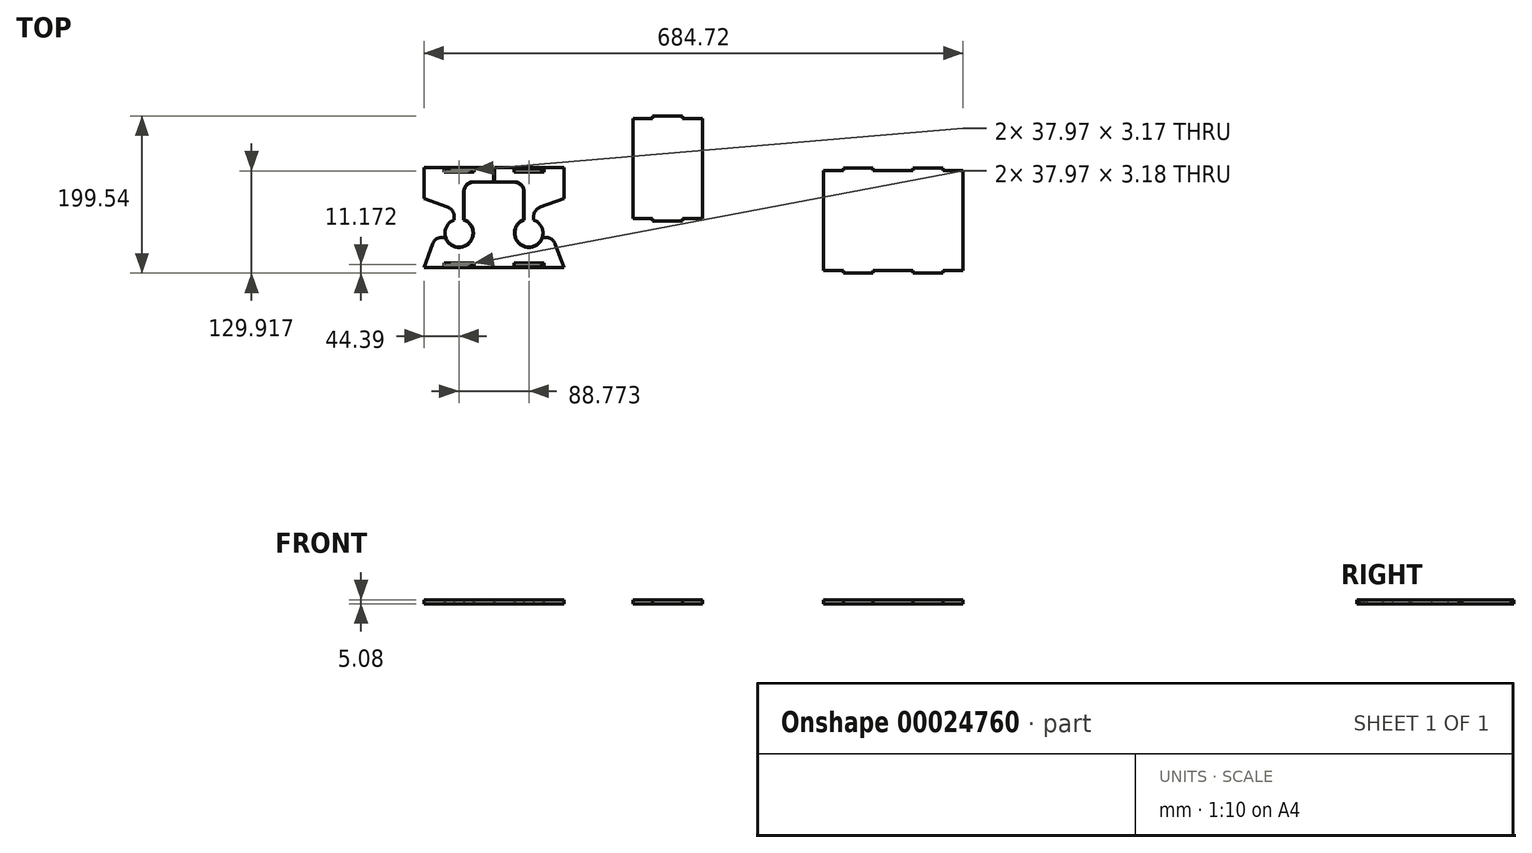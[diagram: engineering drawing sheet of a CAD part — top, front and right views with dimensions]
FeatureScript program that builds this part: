
annotation { "Feature Type Name" : "Feature", "Feature Type Description" : "" }
export const myFeature = defineFeature(function(context is Context, id is Id, definition is map)
    precondition{}
    {
        {
            var Q0;
            Q0=qCreatedBy(makeId("Top.planeOp"),FACE);
            var sketch = newSketch(context, id + "F0", { "sketchPlane" : qUnion([Q0])});
            skLineSegment(sketch, "E0.bottom", {"start": v(44.39, -63.94) * mm, "end": v(-44.39, -63.94) * mm});
            skLineSegment(sketch, "E0.top", {"start": v(43.88, 63.06) * mm, "end": v(-44.39, 63.06) * mm});
            skLineSegment(sketch, "E0.left", {"start": v(44.39, -63.94) * mm, "end": v(44.39, 44.53) * mm, "construction": true});
            skLineSegment(sketch, "E0.right", {"start": v(-44.39, 23.67) * mm, "end": v(-44.39, 63.06) * mm});
            skArc(sketch, "E1", {"start": v(-5.94, -3.24) * mm, "mid": v(0, -37.83) * mm, "end": v(5.94, -3.24) * mm});
            skLineSegment(sketch, "E2", {"start": v(5.94, -3.24) * mm, "end": v(5.94, 32.34) * mm});
            skLineSegment(sketch, "E3", {"start": v(18.64, 45.04) * mm, "end": v(43.88, 45.04) * mm});
            skLineSegment(sketch, "E4", {"start": v(-5.94, -3.24) * mm, "end": v(-5.94, 0.78) * mm});
            skLineSegment(sketch, "E5", {"start": v(-14.3, 12.72) * mm, "end": v(-44.39, 23.67) * mm});
            skLineSegment(sketch, "E6", {"start": v(-44.39, -63.94) * mm, "end": v(-33.44, -33.85) * mm});
            skLineSegment(sketch, "E7", {"start": v(-21.5, -25.5) * mm, "end": v(-17.48, -25.5) * mm});
            skPoint(sketch, "E8.visualSharp", {"position": v(-5.94, 9.68) * mm});
            skArc(sketch, "E8.filletArc", {"start": v(-5.94, 0.78) * mm, "mid": v(-8.24, 8.07) * mm, "end": v(-14.3, 12.72) * mm});
            skPoint(sketch, "E9.visualSharp", {"position": v(-30.4, -25.5) * mm});
            skArc(sketch, "E9.filletArc", {"start": v(-21.5, -25.5) * mm, "mid": v(-28.79, -27.79) * mm, "end": v(-33.44, -33.85) * mm});
            skPoint(sketch, "E10.visualSharp", {"position": v(5.94, 45.04) * mm});
            skArc(sketch, "E10.filletArc", {"start": v(18.64, 45.04) * mm, "mid": v(9.66, 41.32) * mm, "end": v(5.94, 32.34) * mm});
            skArc(sketch, "E11", {"start": v(-16.94, -25.5) * mm, "mid": v(12.41, -32.79) * mm, "end": v(5.94, -3.24) * mm});
            skLineSegment(sketch, "E12.0", {"start": v(18.64, 44.53) * mm, "end": v(44.39, 44.53) * mm});
            skArc(sketch, "E12.1", {"start": v(18.64, 44.53) * mm, "mid": v(10.02, 40.96) * mm, "end": v(6.45, 32.34) * mm});
            skLineSegment(sketch, "E12.2", {"start": v(6.45, -2.89) * mm, "end": v(6.45, 32.34) * mm});
            skArc(sketch, "E12.3", {"start": v(-17.48, -25.5) * mm, "mid": v(12.58, -33.33) * mm, "end": v(6.45, -2.89) * mm});
            skLineSegment(sketch, "E13.bottom", {"start": v(-18.99, -61.4) * mm, "end": v(18.99, -61.4) * mm});
            skLineSegment(sketch, "E13.top", {"start": v(-18.99, -58.22) * mm, "end": v(18.99, -58.22) * mm});
            skLineSegment(sketch, "E13.left", {"start": v(-18.99, -61.4) * mm, "end": v(-18.99, -58.22) * mm});
            skLineSegment(sketch, "E13.right", {"start": v(18.99, -61.4) * mm, "end": v(18.99, -58.22) * mm});
            skLineSegment(sketch, "E14.bottom", {"start": v(-18.99, 60.52) * mm, "end": v(18.99, 60.52) * mm});
            skLineSegment(sketch, "E14.top", {"start": v(-18.99, 57.35) * mm, "end": v(18.99, 57.35) * mm});
            skLineSegment(sketch, "E14.left", {"start": v(-18.99, 60.52) * mm, "end": v(-18.99, 57.35) * mm});
            skLineSegment(sketch, "E14.right", {"start": v(18.99, 60.52) * mm, "end": v(18.99, 57.35) * mm});
            skLineSegment(sketch, "E15", {"start": v(0, 57.35) * mm, "end": v(0, -61.4) * mm, "construction": true});
            skLineSegment(sketch, "E16", {"start": v(43.88, 45.04) * mm, "end": v(43.88, 63.06) * mm});
            skLineSegment(sketch, "E17.MirrorCS", {"start": v(107.76, 57.35) * mm, "end": v(69.79, 57.35) * mm});
            skLineSegment(sketch, "E18.MirrorCS", {"start": v(107.76, -61.4) * mm, "end": v(107.76, -58.22) * mm});
            skLineSegment(sketch, "E19.MirrorCS", {"start": v(107.76, 60.52) * mm, "end": v(107.76, 57.35) * mm});
            skArc(sketch, "E20.MirrorCS", {"start": v(106.25, -25.5) * mm, "mid": v(76.2, -33.33) * mm, "end": v(82.32, -2.89) * mm});
            skLineSegment(sketch, "E21.MirrorCS", {"start": v(133.16, 23.67) * mm, "end": v(133.16, 63.06) * mm});
            skLineSegment(sketch, "E22.MirrorCS", {"start": v(69.79, -61.4) * mm, "end": v(69.79, -58.22) * mm});
            skLineSegment(sketch, "E23.MirrorCS", {"start": v(107.76, -61.4) * mm, "end": v(69.79, -61.4) * mm});
            skLineSegment(sketch, "E24.MirrorCS", {"start": v(82.32, -2.89) * mm, "end": v(82.32, 32.34) * mm});
            skLineSegment(sketch, "E25.MirrorCS", {"start": v(44.9, 45.04) * mm, "end": v(44.9, 63.06) * mm});
            skLineSegment(sketch, "E26.MirrorCS", {"start": v(88.77, 57.35) * mm, "end": v(88.77, -61.4) * mm, "construction": true});
            skLineSegment(sketch, "E27.MirrorCS", {"start": v(107.76, -58.22) * mm, "end": v(69.79, -58.22) * mm});
            skPoint(sketch, "E28.MirrorP", {"position": v(119.17, -25.5) * mm});
            skArc(sketch, "E29.MirrorCS", {"start": v(70.13, 45.04) * mm, "mid": v(79.1, 41.32) * mm, "end": v(82.83, 32.34) * mm});
            skArc(sketch, "E30.MirrorCS", {"start": v(105.5, -13.91) * mm, "mid": v(81.19, -36.13) * mm, "end": v(82.83, -3.24) * mm});
            skLineSegment(sketch, "E31.MirrorCS", {"start": v(70.13, 45.04) * mm, "end": v(44.9, 45.04) * mm});
            skLineSegment(sketch, "E32.MirrorCS", {"start": v(110.27, -25.5) * mm, "end": v(106.25, -25.5) * mm});
            skLineSegment(sketch, "E33.MirrorCS", {"start": v(44.39, -63.94) * mm, "end": v(133.16, -63.94) * mm});
            skPoint(sketch, "E34.MirrorP", {"position": v(94.72, 9.68) * mm});
            skArc(sketch, "E35.MirrorCS", {"start": v(94.72, -3.24) * mm, "mid": v(88.77, -37.83) * mm, "end": v(82.83, -3.24) * mm});
            skLineSegment(sketch, "E36.MirrorCS", {"start": v(107.76, 60.52) * mm, "end": v(69.79, 60.52) * mm});
            skLineSegment(sketch, "E37.MirrorCS", {"start": v(133.16, -63.94) * mm, "end": v(122.2, -33.85) * mm});
            skArc(sketch, "E38.MirrorCS", {"start": v(94.72, 0.78) * mm, "mid": v(97.01, 8.07) * mm, "end": v(103.07, 12.72) * mm});
            skPoint(sketch, "E39.MirrorP", {"position": v(82.83, 45.04) * mm});
            skArc(sketch, "E40.MirrorCS", {"start": v(110.27, -25.5) * mm, "mid": v(117.56, -27.79) * mm, "end": v(122.2, -33.85) * mm});
            skLineSegment(sketch, "E41.MirrorCS", {"start": v(69.79, 60.52) * mm, "end": v(69.79, 57.35) * mm});
            skLineSegment(sketch, "E42.MirrorCS", {"start": v(94.72, -3.24) * mm, "end": v(94.72, 0.78) * mm});
            skLineSegment(sketch, "E43.MirrorCS", {"start": v(70.13, 44.53) * mm, "end": v(44.39, 44.53) * mm});
            skLineSegment(sketch, "E44.MirrorCS", {"start": v(82.83, -3.24) * mm, "end": v(82.83, 32.34) * mm});
            skLineSegment(sketch, "E45.MirrorCS", {"start": v(44.9, 63.06) * mm, "end": v(133.16, 63.06) * mm});
            skLineSegment(sketch, "E46.MirrorCS", {"start": v(103.07, 12.72) * mm, "end": v(133.16, 23.67) * mm});
            skArc(sketch, "E47.MirrorCS", {"start": v(70.13, 44.53) * mm, "mid": v(78.75, 40.96) * mm, "end": v(82.32, 32.34) * mm});
            skLineSegment(sketch, "E48.bottom", {"start": v(246.01, 128.56) * mm, "end": v(284.24, 128.56) * mm});
            skLineSegment(sketch, "E48.top", {"start": v(246.01, -4.79) * mm, "end": v(284.24, -4.79) * mm});
            skLineSegment(sketch, "E48.left", {"start": v(220.93, 125.39) * mm, "end": v(220.93, -1.61) * mm});
            skLineSegment(sketch, "E48.right", {"start": v(309.32, 125.39) * mm, "end": v(309.32, -1.61) * mm});
            skLineSegment(sketch, "E49.left", {"start": v(246.01, 128.56) * mm, "end": v(246.01, 125.39) * mm});
            skLineSegment(sketch, "E49.right", {"start": v(284.24, 128.56) * mm, "end": v(284.24, 125.39) * mm});
            skPoint(sketch, "E50", {"position": v(265.13, 128.56) * mm});
            skLineSegment(sketch, "E51", {"start": v(246.01, 125.39) * mm, "end": v(220.93, 125.39) * mm});
            skLineSegment(sketch, "E52", {"start": v(220.93, 125.39) * mm, "end": v(246.01, 125.39) * mm});
            skLineSegment(sketch, "E53", {"start": v(220.93, 61.89) * mm, "end": v(309.32, 61.89) * mm, "construction": true});
            skPoint(sketch, "E54.orphan", {"position": v(220.93, 128.56) * mm});
            skLineSegment(sketch, "E55.trimOffspring", {"start": v(284.24, 125.39) * mm, "end": v(309.32, 125.39) * mm});
            skPoint(sketch, "E56.orphan", {"position": v(309.32, 128.56) * mm});
            skLineSegment(sketch, "E57.MirrorCS", {"start": v(284.24, -4.79) * mm, "end": v(284.24, -1.61) * mm});
            skLineSegment(sketch, "E58.MirrorCS", {"start": v(246.01, -4.79) * mm, "end": v(246.01, -1.61) * mm});
            skPoint(sketch, "E59.MirrorP", {"position": v(265.13, -4.79) * mm});
            skLineSegment(sketch, "E60.MirrorCS", {"start": v(220.93, -1.61) * mm, "end": v(246.01, -1.61) * mm});
            skLineSegment(sketch, "E61.MirrorCS", {"start": v(246.01, -1.61) * mm, "end": v(220.93, -1.61) * mm});
            skPoint(sketch, "E62.MirrorP", {"position": v(220.93, -4.79) * mm});
            skLineSegment(sketch, "E63.MirrorCS", {"start": v(309.32, -1.61) * mm, "end": v(309.32, 125.39) * mm});
            skLineSegment(sketch, "E64.MirrorCS", {"start": v(284.24, -1.61) * mm, "end": v(309.32, -1.61) * mm});
            skLineSegment(sketch, "E65.MirrorCS", {"start": v(220.93, -1.61) * mm, "end": v(220.93, 125.39) * mm});
            skPoint(sketch, "E66.MirrorP", {"position": v(309.32, -4.79) * mm});
            skPoint(sketch, "E67.MirrorP", {"position": v(462.78, -70.98) * mm});
            skPoint(sketch, "E68.MirrorP", {"position": v(507.17, -70.98) * mm});
            skLineSegment(sketch, "E69", {"start": v(462.78, -4.3) * mm, "end": v(551.56, -4.3) * mm, "construction": true});
            skLineSegment(sketch, "E70.MirrorCS", {"start": v(488.18, -70.98) * mm, "end": v(526.16, -70.98) * mm});
            skPoint(sketch, "E71.MirrorP", {"position": v(551.56, -70.98) * mm});
            skLineSegment(sketch, "E72.MirrorCS", {"start": v(526.16, -67.8) * mm, "end": v(551.56, -67.8) * mm});
            skLineSegment(sketch, "E73.right", {"start": v(551.56, 59.2) * mm, "end": v(551.56, -67.8) * mm, "construction": true});
            skLineSegment(sketch, "E74.MirrorCS", {"start": v(462.78, -67.8) * mm, "end": v(462.78, 59.2) * mm});
            skLineSegment(sketch, "E75.trimOffspring", {"start": v(526.16, 59.2) * mm, "end": v(551.56, 59.2) * mm});
            skPoint(sketch, "E76.orphan", {"position": v(551.56, 62.37) * mm});
            skPoint(sketch, "E77.orphan", {"position": v(462.78, 62.37) * mm});
            skPoint(sketch, "E78", {"position": v(507.17, 62.37) * mm});
            skLineSegment(sketch, "E79.MirrorCS", {"start": v(462.78, -67.8) * mm, "end": v(488.18, -67.8) * mm});
            skLineSegment(sketch, "E80", {"start": v(488.18, 59.2) * mm, "end": v(462.78, 59.2) * mm});
            skLineSegment(sketch, "E73.bottom", {"start": v(488.18, 62.37) * mm, "end": v(526.16, 62.37) * mm});
            skLineSegment(sketch, "E73.left", {"start": v(462.78, 59.2) * mm, "end": v(462.78, -67.8) * mm});
            skLineSegment(sketch, "E81.MirrorCS", {"start": v(551.56, -67.8) * mm, "end": v(551.56, 59.2) * mm, "construction": true});
            skLineSegment(sketch, "E82", {"start": v(462.78, 59.2) * mm, "end": v(488.18, 59.2) * mm});
            skLineSegment(sketch, "E83.MirrorCS", {"start": v(488.18, -67.8) * mm, "end": v(462.78, -67.8) * mm});
            skLineSegment(sketch, "E84.left", {"start": v(488.18, 62.37) * mm, "end": v(488.18, 59.2) * mm});
            skLineSegment(sketch, "E84.right", {"start": v(526.16, 62.37) * mm, "end": v(526.16, 59.2) * mm});
            skLineSegment(sketch, "E85.MirrorCS", {"start": v(488.18, -67.8) * mm, "end": v(488.18, -70.98) * mm});
            skLineSegment(sketch, "E86.MirrorCS", {"start": v(526.16, -67.8) * mm, "end": v(526.16, -70.98) * mm});
            skLineSegment(sketch, "E87.MirrorCS", {"start": v(576.96, -70.98) * mm, "end": v(576.96, -67.8) * mm});
            skLineSegment(sketch, "E88.MirrorCS", {"start": v(614.93, -70.98) * mm, "end": v(614.93, -67.8) * mm});
            skLineSegment(sketch, "E89.MirrorCS", {"start": v(576.96, 62.37) * mm, "end": v(576.96, 59.2) * mm});
            skLineSegment(sketch, "E90.MirrorCS", {"start": v(614.93, 62.37) * mm, "end": v(614.93, 59.2) * mm});
            skLineSegment(sketch, "E91.MirrorCS", {"start": v(614.93, -70.98) * mm, "end": v(576.96, -70.98) * mm});
            skLineSegment(sketch, "E92.MirrorCS", {"start": v(640.33, 59.2) * mm, "end": v(640.33, -67.8) * mm});
            skPoint(sketch, "E93.MirrorP", {"position": v(640.33, -70.98) * mm});
            skLineSegment(sketch, "E94.MirrorCS", {"start": v(614.93, 62.37) * mm, "end": v(576.96, 62.37) * mm});
            skLineSegment(sketch, "E95.MirrorCS", {"start": v(640.33, 59.2) * mm, "end": v(614.93, 59.2) * mm});
            skPoint(sketch, "E96.MirrorP", {"position": v(595.94, 62.37) * mm});
            skLineSegment(sketch, "E97.MirrorCS", {"start": v(614.93, -67.8) * mm, "end": v(640.33, -67.8) * mm});
            skPoint(sketch, "E98.MirrorP", {"position": v(595.94, -70.98) * mm});
            skLineSegment(sketch, "E99.MirrorCS", {"start": v(576.96, -67.8) * mm, "end": v(551.56, -67.8) * mm});
            skPoint(sketch, "E100.MirrorP", {"position": v(640.33, 62.37) * mm});
            skLineSegment(sketch, "E101.MirrorCS", {"start": v(640.33, -67.8) * mm, "end": v(640.33, 59.2) * mm});
            skLineSegment(sketch, "E102.MirrorCS", {"start": v(614.93, 59.2) * mm, "end": v(640.33, 59.2) * mm});
            skLineSegment(sketch, "E103.MirrorCS", {"start": v(640.33, -67.8) * mm, "end": v(614.93, -67.8) * mm});
            skLineSegment(sketch, "E104.MirrorCS", {"start": v(640.33, -4.3) * mm, "end": v(551.56, -4.3) * mm, "construction": true});
            skLineSegment(sketch, "E105.MirrorCS", {"start": v(576.96, 59.2) * mm, "end": v(551.56, 59.2) * mm});
            skPoint(sketch, "E106", {"position": v(104.67, -28.03) * mm});
            skLineSegment(sketch, "E107.trimOffspring", {"start": v(322.72, -47.2) * mm, "end": v(347.8, -47.2) * mm});
            skPoint(sketch, "E108.orphan", {"position": v(347.8, -177.38) * mm});
            skLineSegment(sketch, "E109.MirrorCS", {"start": v(322.72, -174.2) * mm, "end": v(347.8, -174.2) * mm});
            skPoint(sketch, "E110.orphan", {"position": v(259.4, -44.03) * mm});
            skLineSegment(sketch, "E111.MirrorCS", {"start": v(259.4, -174.2) * mm, "end": v(259.4, -47.2) * mm});
            skPoint(sketch, "E112", {"position": v(303.6, -44.03) * mm});
            skPoint(sketch, "E113.orphan", {"position": v(347.8, -44.03) * mm});
            skLineSegment(sketch, "E114.MirrorCS", {"start": v(284.49, -177.38) * mm, "end": v(322.72, -177.38) * mm});
            skLineSegment(sketch, "E115.MirrorCS", {"start": v(284.49, -174.2) * mm, "end": v(259.4, -174.2) * mm});
            skPoint(sketch, "E116.MirrorP", {"position": v(259.4, -177.38) * mm});
            skLineSegment(sketch, "E117", {"start": v(259.4, -47.2) * mm, "end": v(284.49, -47.2) * mm});
            skLineSegment(sketch, "E118.bottom", {"start": v(284.49, -44.03) * mm, "end": v(322.72, -44.03) * mm});
            skLineSegment(sketch, "E119.MirrorCS", {"start": v(347.8, -174.2) * mm, "end": v(347.8, -47.2) * mm});
            skPoint(sketch, "E120.MirrorP", {"position": v(303.6, -177.38) * mm});
            skLineSegment(sketch, "E121", {"start": v(259.4, -110.7) * mm, "end": v(347.8, -110.7) * mm, "construction": true});
            skLineSegment(sketch, "E118.left", {"start": v(259.4, -47.2) * mm, "end": v(259.4, -174.2) * mm});
            skLineSegment(sketch, "E118.right", {"start": v(347.8, -47.2) * mm, "end": v(347.8, -174.2) * mm});
            skLineSegment(sketch, "E122.MirrorCS", {"start": v(259.4, -174.2) * mm, "end": v(284.49, -174.2) * mm});
            skLineSegment(sketch, "E123", {"start": v(284.49, -47.2) * mm, "end": v(259.4, -47.2) * mm});
            skLineSegment(sketch, "E124.MirrorCS", {"start": v(322.72, -177.38) * mm, "end": v(322.72, -174.2) * mm});
            skLineSegment(sketch, "E125.left", {"start": v(284.49, -44.03) * mm, "end": v(284.49, -47.2) * mm});
            skLineSegment(sketch, "E126.MirrorCS", {"start": v(284.49, -177.38) * mm, "end": v(284.49, -174.2) * mm});
            skLineSegment(sketch, "E125.right", {"start": v(322.72, -44.03) * mm, "end": v(322.72, -47.2) * mm});
            skLineSegment(sketch, "E127.MirrorCS", {"start": v(-22.32, -274.1) * mm, "end": v(-60.3, -274.1) * mm});
            skLineSegment(sketch, "E128.MirrorCS", {"start": v(-27, -203.24) * mm, "end": v(3.22, -192.24) * mm});
            skArc(sketch, "E129.MirrorCS", {"start": v(-23.78, -241.23) * mm, "mid": v(-53.77, -249.37) * mm, "end": v(-47.76, -218.88) * mm});
            skPoint(sketch, "E130.MirrorP", {"position": v(-10.83, -241.23) * mm});
            skLineSegment(sketch, "E131.MirrorCS", {"start": v(-22.32, -158.52) * mm, "end": v(-60.3, -158.52) * mm});
            skArc(sketch, "E132.MirrorCS", {"start": v(-35.36, -219.24) * mm, "mid": v(-41.3, -253.78) * mm, "end": v(-47.25, -219.24) * mm});
            skArc(sketch, "E133.3", {"start": v(-147.6, -241.23) * mm, "mid": v(-117.6, -249.37) * mm, "end": v(-123.63, -218.88) * mm});
            skLineSegment(sketch, "E134.MirrorCS", {"start": v(-22.32, -155.35) * mm, "end": v(-60.3, -155.35) * mm});
            skLineSegment(sketch, "E135.MirrorCS", {"start": v(-59.95, -170.95) * mm, "end": v(-85.18, -170.95) * mm});
            skLineSegment(sketch, "E136.MirrorCS", {"start": v(-85.7, -279.8) * mm, "end": v(3.22, -279.8) * mm});
            skLineSegment(sketch, "E137", {"start": v(-86.2, -170.95) * mm, "end": v(-86.2, -152.8) * mm});
            skPoint(sketch, "E138.MirrorP", {"position": v(-35.36, -206.28) * mm});
            skLineSegment(sketch, "E139.MirrorCS", {"start": v(-41.3, -158.52) * mm, "end": v(-41.3, -277.27) * mm, "construction": true});
            skLineSegment(sketch, "E140.MirrorCS", {"start": v(-85.18, -152.8) * mm, "end": v(3.22, -152.8) * mm});
            skLineSegment(sketch, "E133.2", {"start": v(-123.63, -218.88) * mm, "end": v(-123.63, -183.65) * mm});
            skPoint(sketch, "E141.visualSharp", {"position": v(-136.02, -206.28) * mm});
            skLineSegment(sketch, "E142", {"start": v(-130.08, -158.52) * mm, "end": v(-130.08, -277.27) * mm, "construction": true});
            skLineSegment(sketch, "E143.bottom", {"start": v(-149.06, -155.35) * mm, "end": v(-111.1, -155.35) * mm});
            skPoint(sketch, "E144", {"position": v(-25.43, -244) * mm});
            skLineSegment(sketch, "E143.top", {"start": v(-149.06, -158.52) * mm, "end": v(-111.1, -158.52) * mm});
            skLineSegment(sketch, "E145.MirrorCS", {"start": v(-85.18, -170.95) * mm, "end": v(-85.18, -152.8) * mm});
            skLineSegment(sketch, "E146.MirrorCS", {"start": v(-47.25, -219.24) * mm, "end": v(-47.25, -183.65) * mm});
            skPoint(sketch, "E147.visualSharp", {"position": v(-124.13, -170.95) * mm});
            skLineSegment(sketch, "E148.top", {"start": v(-149.06, -274.1) * mm, "end": v(-111.1, -274.1) * mm});
            skLineSegment(sketch, "E149.MirrorCS", {"start": v(-22.32, -277.27) * mm, "end": v(-60.3, -277.27) * mm});
            skLineSegment(sketch, "E148.bottom", {"start": v(-149.06, -277.27) * mm, "end": v(-111.1, -277.27) * mm});
            skPoint(sketch, "E150.visualSharp", {"position": v(-160.56, -241.23) * mm});
            skLineSegment(sketch, "E151.MirrorCS", {"start": v(3.22, -192.24) * mm, "end": v(3.22, -152.8) * mm});
            skPoint(sketch, "E152.MirrorP", {"position": v(-47.25, -170.95) * mm});
            skLineSegment(sketch, "E153", {"start": v(-174.6, -279.8) * mm, "end": v(-163.6, -249.59) * mm});
            skLineSegment(sketch, "E154", {"start": v(-144.38, -203.24) * mm, "end": v(-174.6, -192.24) * mm});
            skArc(sketch, "E155", {"start": v(-136.02, -219.24) * mm, "mid": v(-130.08, -253.78) * mm, "end": v(-124.13, -219.24) * mm});
            skLineSegment(sketch, "E156.right", {"start": v(-174.6, -192.24) * mm, "end": v(-174.6, -152.8) * mm});
            skLineSegment(sketch, "E156.left", {"start": v(-85.7, -279.8) * mm, "end": v(-85.7, -171.46) * mm, "construction": true});
            skLineSegment(sketch, "E156.top", {"start": v(-86.2, -152.8) * mm, "end": v(-174.6, -152.8) * mm});
            skLineSegment(sketch, "E156.bottom", {"start": v(-85.7, -279.8) * mm, "end": v(-174.6, -279.8) * mm});
            skLineSegment(sketch, "E157.MirrorCS", {"start": v(3.22, -279.8) * mm, "end": v(-7.78, -249.59) * mm});
            skArc(sketch, "E158.MirrorCS", {"start": v(-35.36, -215.18) * mm, "mid": v(-33.06, -207.9) * mm, "end": v(-27, -203.24) * mm});
            skArc(sketch, "E133.1", {"start": v(-111.43, -171.46) * mm, "mid": v(-120.05, -175.03) * mm, "end": v(-123.63, -183.65) * mm});
            skLineSegment(sketch, "E159", {"start": v(-111.43, -170.95) * mm, "end": v(-86.2, -170.95) * mm});
            skArc(sketch, "E160.MirrorCS", {"start": v(-24.6, -229.9) * mm, "mid": v(-48.87, -252.08) * mm, "end": v(-47.25, -219.24) * mm});
            skArc(sketch, "E161.MirrorCS", {"start": v(-59.95, -170.95) * mm, "mid": v(-50.97, -174.67) * mm, "end": v(-47.25, -183.65) * mm});
            skLineSegment(sketch, "E162.MirrorCS", {"start": v(-47.76, -218.88) * mm, "end": v(-47.76, -183.65) * mm});
            skLineSegment(sketch, "E163.MirrorCS", {"start": v(-59.95, -171.46) * mm, "end": v(-85.7, -171.46) * mm});
            skArc(sketch, "E164.MirrorCS", {"start": v(-19.72, -241.23) * mm, "mid": v(-12.43, -243.53) * mm, "end": v(-7.78, -249.59) * mm});
            skLineSegment(sketch, "E165", {"start": v(-124.13, -219.24) * mm, "end": v(-124.13, -183.65) * mm});
            skArc(sketch, "E166", {"start": v(-147.07, -241.23) * mm, "mid": v(-117.77, -248.83) * mm, "end": v(-124.13, -219.24) * mm});
            skArc(sketch, "E147.filletArc", {"start": v(-111.43, -170.95) * mm, "mid": v(-120.41, -174.67) * mm, "end": v(-124.13, -183.65) * mm});
            skLineSegment(sketch, "E167.MirrorCS", {"start": v(-60.3, -155.35) * mm, "end": v(-60.3, -158.52) * mm});
            skLineSegment(sketch, "E168.MirrorCS", {"start": v(-22.32, -277.27) * mm, "end": v(-22.32, -274.1) * mm});
            skLineSegment(sketch, "E143.right", {"start": v(-111.1, -155.35) * mm, "end": v(-111.1, -158.52) * mm});
            skLineSegment(sketch, "E143.left", {"start": v(-149.06, -155.35) * mm, "end": v(-149.06, -158.52) * mm});
            skArc(sketch, "E169.MirrorCS", {"start": v(-59.95, -171.46) * mm, "mid": v(-51.33, -175.03) * mm, "end": v(-47.76, -183.65) * mm});
            skLineSegment(sketch, "E148.left", {"start": v(-149.06, -277.27) * mm, "end": v(-149.06, -274.1) * mm});
            skLineSegment(sketch, "E170.MirrorCS", {"start": v(-35.36, -219.24) * mm, "end": v(-35.36, -215.18) * mm});
            skLineSegment(sketch, "E171.MirrorCS", {"start": v(-60.3, -277.27) * mm, "end": v(-60.3, -274.1) * mm});
            skArc(sketch, "E150.filletArc", {"start": v(-151.66, -241.23) * mm, "mid": v(-158.95, -243.53) * mm, "end": v(-163.6, -249.59) * mm});
            skArc(sketch, "E141.filletArc", {"start": v(-136.02, -215.18) * mm, "mid": v(-138.32, -207.9) * mm, "end": v(-144.38, -203.24) * mm});
            skLineSegment(sketch, "E133.0", {"start": v(-111.43, -171.46) * mm, "end": v(-85.7, -171.46) * mm});
            skLineSegment(sketch, "E172.MirrorCS", {"start": v(-22.32, -155.35) * mm, "end": v(-22.32, -158.52) * mm});
            skLineSegment(sketch, "E173.MirrorCS", {"start": v(-19.72, -241.23) * mm, "end": v(-23.78, -241.23) * mm});
            skLineSegment(sketch, "E148.right", {"start": v(-111.1, -277.27) * mm, "end": v(-111.1, -274.1) * mm});
            skLineSegment(sketch, "E174", {"start": v(-151.66, -241.23) * mm, "end": v(-147.6, -241.23) * mm});
            skLineSegment(sketch, "E175", {"start": v(-136.02, -219.24) * mm, "end": v(-136.02, -215.18) * mm});
            skSolve(sketch);
        }
        {
            var Q0;
            Q0=makeQuery(id+"F0.imprint","IMPRINT",FACE,{"disambiguationData":[TD([[makeQuery(id+"F0.imprint","IMPRINT",EDGE,{"derivedFrom":sQuery(id+"F0.wireOp",EDGE,"E0.bottom")}),-1.0]])]});
            var Q1;
            Q1=makeQuery(id+"F0.imprint","IMPRINT",FACE,{"disambiguationData":[TD([[makeQuery(id+"F0.imprint","IMPRINT",EDGE,{"derivedFrom":sQuery(id+"F0.wireOp",EDGE,"E17.MirrorCS")}),1.0]])]});
            var Q2;
            Q2=makeQuery(id+"F0.imprint","IMPRINT",FACE,{"disambiguationData":[TD([[makeQuery(id+"F0.imprint","IMPRINT",EDGE,{"derivedFrom":sQuery(id+"F0.wireOp",EDGE,"E0.top")}),1.0]])]});
            var Q3;
            Q3=makeQuery(id+"F0.imprint","IMPRINT",FACE,{"disambiguationData":[TD([[makeQuery(id+"F0.imprint","IMPRINT",EDGE,{"derivedFrom":sQuery(id+"F0.wireOp",EDGE,"E48.bottom")}),-1.0]])]});
            var Q4;
            Q4=makeQuery(id+"F0.imprint","IMPRINT",FACE,{"disambiguationData":[TD([[makeQuery(id+"F0.imprint","IMPRINT",EDGE,{"derivedFrom":sQuery(id+"F0.wireOp",EDGE,"E72.MirrorCS")}),1.0]])]});
            var Q5;
            Q5=makeQuery(id+"F0.imprint","IMPRINT",FACE,{"disambiguationData":[TD([[makeQuery(id+"F0.imprint","IMPRINT",EDGE,{"derivedFrom":sQuery(id+"F0.wireOp",EDGE,"E81.MirrorCS")}),-1.0]])]});
            extrude(context, id + "F1", {"entities" : qUnion([Q0, Q1, Q2, Q3, Q4, Q5]), "depth" : 5.08 * mm});
        }
    });
